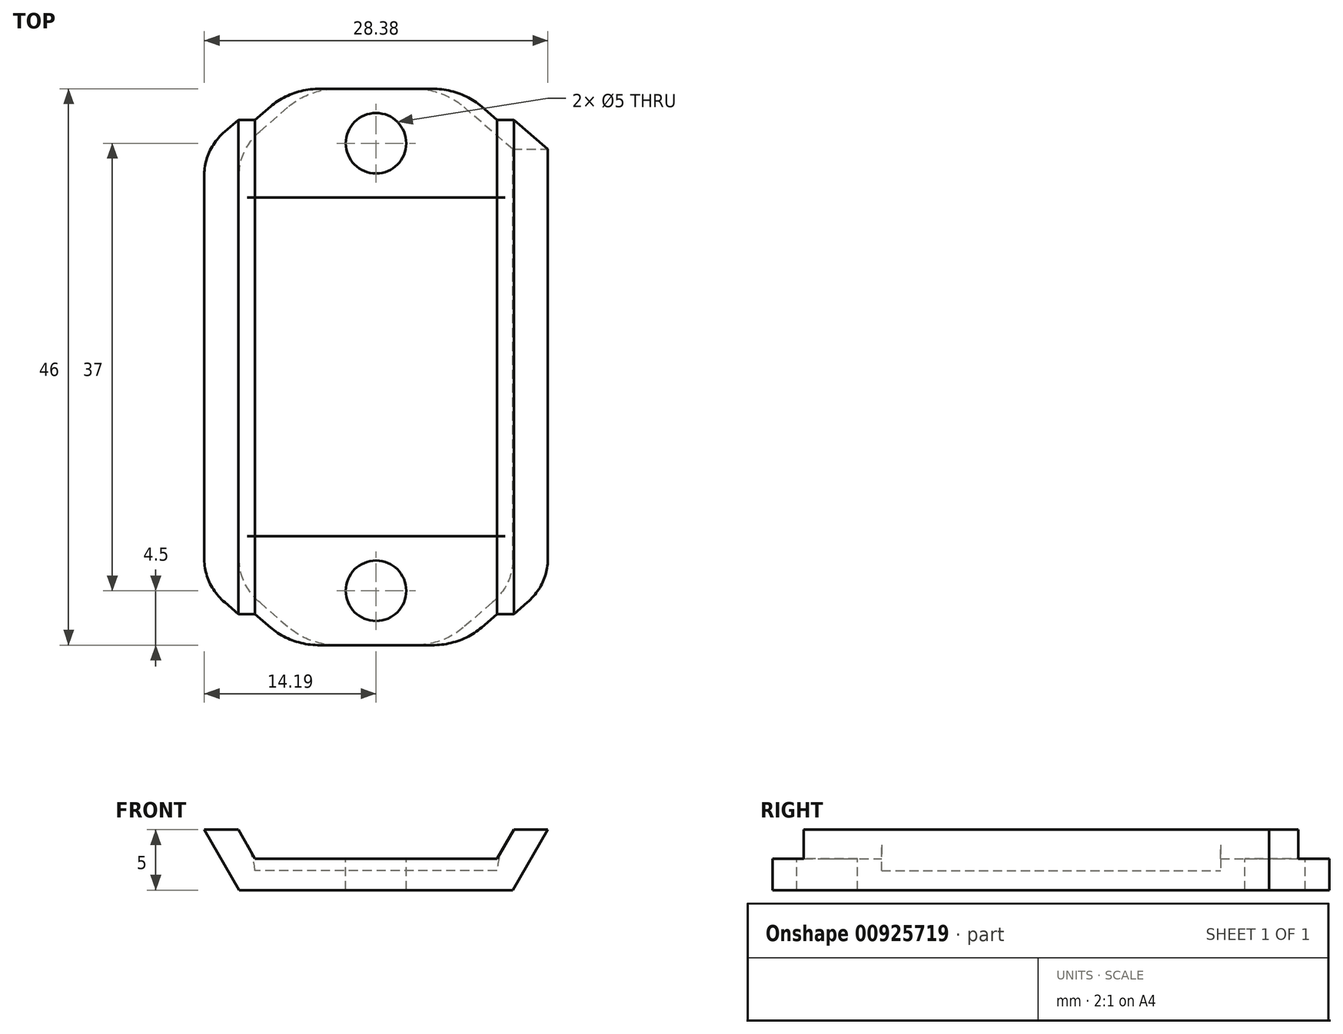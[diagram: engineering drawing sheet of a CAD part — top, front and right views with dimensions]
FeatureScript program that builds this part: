
annotation { "Feature Type Name" : "Feature", "Feature Type Description" : "" }
export const myFeature = defineFeature(function(context is Context, id is Id, definition is map)
    precondition{}
    {
        {
            var Q0;
            Q0=qCreatedBy(makeId("Front.planeOp"),FACE);
            var sketch = newSketch(context, id + "F0", { "sketchPlane" : qUnion([Q0])});
            skLineSegment(sketch, "E0", {"start": v(0, 0) * mm, "end": v(-11.3, 0) * mm});
            skLineSegment(sketch, "E1", {"start": v(-11.3, 0) * mm, "end": v(-14.19, 5) * mm});
            skLineSegment(sketch, "E2", {"start": v(-14.19, 5) * mm, "end": v(-11.39, 5) * mm});
            skLineSegment(sketch, "E3", {"start": v(-11.39, 5) * mm, "end": v(-10, 2.6) * mm});
            skLineSegment(sketch, "E4", {"start": v(-10, 2.6) * mm, "end": v(0, 2.6) * mm});
            skLineSegment(sketch, "E5", {"start": v(0, -9.75) * mm, "end": v(0, 12.13) * mm, "construction": true});
            skLineSegment(sketch, "E6.MirrorCS", {"start": v(10, 2.6) * mm, "end": v(0, 2.6) * mm});
            skLineSegment(sketch, "E7.MirrorCS", {"start": v(11.39, 5) * mm, "end": v(10, 2.6) * mm});
            skLineSegment(sketch, "E8.MirrorCS", {"start": v(14.19, 5) * mm, "end": v(11.39, 5) * mm});
            skLineSegment(sketch, "E9.MirrorCS", {"start": v(11.3, 0) * mm, "end": v(14.19, 5) * mm});
            skLineSegment(sketch, "E10.MirrorCS", {"start": v(0, 0) * mm, "end": v(11.3, 0) * mm});
            skSolve(sketch);
        }
        {
            var Q0;
            Q0=makeQuery(id+"F0.imprint","IMPRINT",FACE,{"disambiguationData":[TD([[makeQuery(id+"F0.imprint","IMPRINT",EDGE,{"derivedFrom":sQuery(id+"F0.wireOp",EDGE,"E0")}),-1.0]])]});
            extrude(context, id + "F1", {"entities" : qUnion([Q0]), "endBound" : BoundingType.SYMMETRIC, "depth" : 2 * (13 * mm + 10 * mm), "offsetDistance" : 25 * mm});
        }
        {
            var Q0;
            Q0=makeQuery(id+"F1.opExtrude","SWEPT_FACE",FACE,{"disambiguationData":[OSD([sQuery(id+"F0.wireOp",EDGE,"E4"),sQuery(id+"F0.wireOp",EDGE,"E6.MirrorCS")])]});
            var sketch = newSketch(context, id + "F2", { "sketchPlane" : qUnion([Q0])});
            skLineSegment(sketch, "E11.bottom", {"start": v(10, 14) * mm, "end": v(-10, 14) * mm});
            skLineSegment(sketch, "E11.top", {"start": v(10, -14) * mm, "end": v(-10, -14) * mm});
            skLineSegment(sketch, "E11.left", {"start": v(10, 14) * mm, "end": v(10, -14) * mm});
            skLineSegment(sketch, "E11.right", {"start": v(-10, 14) * mm, "end": v(-10, -14) * mm});
            skPoint(sketch, "E11.middle", {"position": v(0, 0) * mm});
            skLineSegment(sketch, "E12", {"start": v(-10, 23) * mm, "end": v(10, 14) * mm, "construction": true});
            skPoint(sketch, "E13", {"position": v(0, 18.5) * mm});
            skLineSegment(sketch, "E14", {"start": v(10, -14) * mm, "end": v(-10, -23) * mm, "construction": true});
            skPoint(sketch, "E15", {"position": v(0, -18.5) * mm});
            skSolve(sketch);
        }
        {
            var Q0;
            Q0=makeQuery(id+"F2.imprint","IMPRINT",FACE,{"disambiguationData":[TD([[makeQuery(id+"F2.imprint","IMPRINT",EDGE,{"derivedFrom":sQuery(id+"F2.wireOp",EDGE,"E11.bottom")}),1.0]])]});
            extrude(context, id + "F3", {"entities" : qUnion([Q0]), "operationType" : NewBodyOperationType.REMOVE, "oppositeDirection" : true, "depth" : 1 * mm, "offsetDistance" : 25 * mm});
        }
        {
            var Q0;
            Q0=sQuery(id+"F2.wireOp",VERTEX,"E15");
            var Q1;
            Q1=sQuery(id+"F2.wireOp",VERTEX,"E13");
            var Q2;
            Q2=makeQuery(id+"F1.opExtrude","SWEPT_BODY",BODY,{"disambiguationData":[OSD([sQuery(id+"F0.wireOp",EDGE,"E0"),sQuery(id+"F0.wireOp",EDGE,"E1"),sQuery(id+"F0.wireOp",EDGE,"E2"),sQuery(id+"F0.wireOp",EDGE,"E3"),sQuery(id+"F0.wireOp",EDGE,"E4"),sQuery(id+"F0.wireOp",EDGE,"E6.MirrorCS"),sQuery(id+"F0.wireOp",EDGE,"E7.MirrorCS"),sQuery(id+"F0.wireOp",EDGE,"E8.MirrorCS"),sQuery(id+"F0.wireOp",EDGE,"E9.MirrorCS"),sQuery(id+"F0.wireOp",EDGE,"E10.MirrorCS")])]});
            hole(context, id + "F4", {"style" : HoleStyle.SIMPLE, "endStyle" : HoleEndStyle.THROUGH, "holeDiameter" : 5 * mm, "majorDiameter" : 5 * mm, "isTappedThrough" : true, "tappedDepth" : 12 * mm, "tapClearance" : 3, "locations" : qUnion([Q0, Q1]), "scope" : qUnion([Q2])});
        }
        {
            var Q0;
            Q0=makeQuery(id+"F1.opExtrude","CAP_EDGE",EDGE,{"disambiguationData":[OSD([sQuery(id+"F0.wireOp",EDGE,"E1")])],"isStart":false});
            var Q1;
            Q1=makeQuery(id+"F1.opExtrude","CAP_EDGE",EDGE,{"disambiguationData":[OSD([sQuery(id+"F0.wireOp",EDGE,"E9.MirrorCS")])],"isStart":false});
            var Q2;
            Q2=makeQuery(id+"F1.opExtrude","CAP_EDGE",EDGE,{"disambiguationData":[OSD([sQuery(id+"F0.wireOp",EDGE,"E1")])],"isStart":true});
            var Q3;
            Q3=makeQuery(id+"F1.opExtrude","CAP_EDGE",EDGE,{"disambiguationData":[OSD([sQuery(id+"F0.wireOp",EDGE,"E9.MirrorCS")])],"isStart":true});
            chamfer(context, id + "F5", {"entities" : qUnion([Q0, Q1, Q2, Q3]), "width" : 5 * mm, "tangentPropagation" : true});
        }
        {
            var Q0;
            Q0=makeQuery(id+"F3.boolean.opBoolean","MERGE",EDGE,{"derivedFrom":[makeQuery(id+"F1.opExtrude","SWEPT_EDGE",EDGE,{"disambiguationData":[OSD([sQuery(id+"F0.wireOp",EDGE,"E3"),sQuery(id+"F0.wireOp",EDGE,"E4")])]})],"fromTools":[makeQuery(id+"F3.opExtrude","CAP_EDGE",EDGE,{"disambiguationData":[OSD([sQuery(id+"F2.wireOp",EDGE,"E11.right")])],"isStart":true})]});
            var Q1;
            Q1=makeQuery(id+"F3.boolean.opBoolean","MERGE",EDGE,{"derivedFrom":[makeQuery(id+"F1.opExtrude","SWEPT_EDGE",EDGE,{"disambiguationData":[OSD([sQuery(id+"F0.wireOp",EDGE,"E6.MirrorCS"),sQuery(id+"F0.wireOp",EDGE,"E7.MirrorCS")])]})],"fromTools":[makeQuery(id+"F3.opExtrude","CAP_EDGE",EDGE,{"disambiguationData":[OSD([sQuery(id+"F2.wireOp",EDGE,"E11.left")])],"isStart":true})]});
            var Q2;
            {var subQ0=sQuery(id+"F0.wireOp",EDGE,"E1");Q2=makeQuery(id+"F5.opChamfer","BLEND_EDGE",EDGE,{"blendedFrom":[makeQuery(id+"F1.opExtrude","CAP_EDGE",EDGE,{"disambiguationData":[OSD([subQ0])],"isStart":true}),makeQuery(id+"F1.opExtrude","CAP_FACE",FACE,{"disambiguationData":[OSD([sQuery(id+"F0.wireOp",EDGE,"E0"),subQ0,sQuery(id+"F0.wireOp",EDGE,"E2"),sQuery(id+"F0.wireOp",EDGE,"E3"),sQuery(id+"F0.wireOp",EDGE,"E4"),sQuery(id+"F0.wireOp",EDGE,"E6.MirrorCS"),sQuery(id+"F0.wireOp",EDGE,"E7.MirrorCS"),sQuery(id+"F0.wireOp",EDGE,"E8.MirrorCS"),sQuery(id+"F0.wireOp",EDGE,"E9.MirrorCS"),sQuery(id+"F0.wireOp",EDGE,"E10.MirrorCS")])],"isStart":true})],"blendedInto":[makeQuery(id+"F1.opExtrude","CAP_FACE",FACE,{"disambiguationData":[OSD([sQuery(id+"F0.wireOp",EDGE,"E0"),subQ0,sQuery(id+"F0.wireOp",EDGE,"E2"),sQuery(id+"F0.wireOp",EDGE,"E3"),sQuery(id+"F0.wireOp",EDGE,"E4"),sQuery(id+"F0.wireOp",EDGE,"E6.MirrorCS"),sQuery(id+"F0.wireOp",EDGE,"E7.MirrorCS"),sQuery(id+"F0.wireOp",EDGE,"E8.MirrorCS"),sQuery(id+"F0.wireOp",EDGE,"E9.MirrorCS"),sQuery(id+"F0.wireOp",EDGE,"E10.MirrorCS")])],"isStart":true})]});}
            var Q3;
            {var subQ0=sQuery(id+"F0.wireOp",EDGE,"E9.MirrorCS");Q3=makeQuery(id+"F5.opChamfer","BLEND_EDGE",EDGE,{"blendedFrom":[makeQuery(id+"F1.opExtrude","CAP_EDGE",EDGE,{"disambiguationData":[OSD([subQ0])],"isStart":true}),makeQuery(id+"F1.opExtrude","CAP_FACE",FACE,{"disambiguationData":[OSD([sQuery(id+"F0.wireOp",EDGE,"E0"),sQuery(id+"F0.wireOp",EDGE,"E1"),sQuery(id+"F0.wireOp",EDGE,"E2"),sQuery(id+"F0.wireOp",EDGE,"E3"),sQuery(id+"F0.wireOp",EDGE,"E4"),sQuery(id+"F0.wireOp",EDGE,"E6.MirrorCS"),sQuery(id+"F0.wireOp",EDGE,"E7.MirrorCS"),sQuery(id+"F0.wireOp",EDGE,"E8.MirrorCS"),subQ0,sQuery(id+"F0.wireOp",EDGE,"E10.MirrorCS")])],"isStart":true})],"blendedInto":[makeQuery(id+"F1.opExtrude","CAP_FACE",FACE,{"disambiguationData":[OSD([sQuery(id+"F0.wireOp",EDGE,"E0"),sQuery(id+"F0.wireOp",EDGE,"E1"),sQuery(id+"F0.wireOp",EDGE,"E2"),sQuery(id+"F0.wireOp",EDGE,"E3"),sQuery(id+"F0.wireOp",EDGE,"E4"),sQuery(id+"F0.wireOp",EDGE,"E6.MirrorCS"),sQuery(id+"F0.wireOp",EDGE,"E7.MirrorCS"),sQuery(id+"F0.wireOp",EDGE,"E8.MirrorCS"),subQ0,sQuery(id+"F0.wireOp",EDGE,"E10.MirrorCS")])],"isStart":true})]});}
            var Q4;
            {var subQ0=sQuery(id+"F0.wireOp",EDGE,"E1");Q4=makeQuery(id+"F5.opChamfer","BLEND_EDGE",EDGE,{"blendedFrom":[makeQuery(id+"F1.opExtrude","CAP_EDGE",EDGE,{"disambiguationData":[OSD([subQ0])],"isStart":true}),makeQuery(id+"F1.opExtrude","SWEPT_FACE",FACE,{"disambiguationData":[OSD([subQ0])]})],"blendedInto":[makeQuery(id+"F1.opExtrude","SWEPT_FACE",FACE,{"disambiguationData":[OSD([subQ0])]})]});}
            var Q5;
            {var subQ0=sQuery(id+"F0.wireOp",EDGE,"E9.MirrorCS");Q5=makeQuery(id+"F5.opChamfer","BLEND_EDGE",EDGE,{"blendedFrom":[makeQuery(id+"F1.opExtrude","CAP_EDGE",EDGE,{"disambiguationData":[OSD([subQ0])],"isStart":false}),makeQuery(id+"F1.opExtrude","SWEPT_FACE",FACE,{"disambiguationData":[OSD([subQ0])]})],"blendedInto":[makeQuery(id+"F1.opExtrude","SWEPT_FACE",FACE,{"disambiguationData":[OSD([subQ0])]})]});}
            var Q6;
            {var subQ0=sQuery(id+"F0.wireOp",EDGE,"E9.MirrorCS");Q6=makeQuery(id+"F5.opChamfer","BLEND_EDGE",EDGE,{"blendedFrom":[makeQuery(id+"F1.opExtrude","CAP_EDGE",EDGE,{"disambiguationData":[OSD([subQ0])],"isStart":false}),makeQuery(id+"F1.opExtrude","CAP_FACE",FACE,{"disambiguationData":[OSD([sQuery(id+"F0.wireOp",EDGE,"E0"),sQuery(id+"F0.wireOp",EDGE,"E1"),sQuery(id+"F0.wireOp",EDGE,"E2"),sQuery(id+"F0.wireOp",EDGE,"E3"),sQuery(id+"F0.wireOp",EDGE,"E4"),sQuery(id+"F0.wireOp",EDGE,"E6.MirrorCS"),sQuery(id+"F0.wireOp",EDGE,"E7.MirrorCS"),sQuery(id+"F0.wireOp",EDGE,"E8.MirrorCS"),subQ0,sQuery(id+"F0.wireOp",EDGE,"E10.MirrorCS")])],"isStart":false})],"blendedInto":[makeQuery(id+"F1.opExtrude","CAP_FACE",FACE,{"disambiguationData":[OSD([sQuery(id+"F0.wireOp",EDGE,"E0"),sQuery(id+"F0.wireOp",EDGE,"E1"),sQuery(id+"F0.wireOp",EDGE,"E2"),sQuery(id+"F0.wireOp",EDGE,"E3"),sQuery(id+"F0.wireOp",EDGE,"E4"),sQuery(id+"F0.wireOp",EDGE,"E6.MirrorCS"),sQuery(id+"F0.wireOp",EDGE,"E7.MirrorCS"),sQuery(id+"F0.wireOp",EDGE,"E8.MirrorCS"),subQ0,sQuery(id+"F0.wireOp",EDGE,"E10.MirrorCS")])],"isStart":false})]});}
            var Q7;
            {var subQ0=sQuery(id+"F0.wireOp",EDGE,"E1");Q7=makeQuery(id+"F5.opChamfer","BLEND_EDGE",EDGE,{"blendedFrom":[makeQuery(id+"F1.opExtrude","CAP_EDGE",EDGE,{"disambiguationData":[OSD([subQ0])],"isStart":false}),makeQuery(id+"F1.opExtrude","CAP_FACE",FACE,{"disambiguationData":[OSD([sQuery(id+"F0.wireOp",EDGE,"E0"),subQ0,sQuery(id+"F0.wireOp",EDGE,"E2"),sQuery(id+"F0.wireOp",EDGE,"E3"),sQuery(id+"F0.wireOp",EDGE,"E4"),sQuery(id+"F0.wireOp",EDGE,"E6.MirrorCS"),sQuery(id+"F0.wireOp",EDGE,"E7.MirrorCS"),sQuery(id+"F0.wireOp",EDGE,"E8.MirrorCS"),sQuery(id+"F0.wireOp",EDGE,"E9.MirrorCS"),sQuery(id+"F0.wireOp",EDGE,"E10.MirrorCS")])],"isStart":false})],"blendedInto":[makeQuery(id+"F1.opExtrude","CAP_FACE",FACE,{"disambiguationData":[OSD([sQuery(id+"F0.wireOp",EDGE,"E0"),subQ0,sQuery(id+"F0.wireOp",EDGE,"E2"),sQuery(id+"F0.wireOp",EDGE,"E3"),sQuery(id+"F0.wireOp",EDGE,"E4"),sQuery(id+"F0.wireOp",EDGE,"E6.MirrorCS"),sQuery(id+"F0.wireOp",EDGE,"E7.MirrorCS"),sQuery(id+"F0.wireOp",EDGE,"E8.MirrorCS"),sQuery(id+"F0.wireOp",EDGE,"E9.MirrorCS"),sQuery(id+"F0.wireOp",EDGE,"E10.MirrorCS")])],"isStart":false})]});}
            var Q8;
            {var subQ0=sQuery(id+"F0.wireOp",EDGE,"E1");Q8=makeQuery(id+"F5.opChamfer","BLEND_EDGE",EDGE,{"blendedFrom":[makeQuery(id+"F1.opExtrude","CAP_EDGE",EDGE,{"disambiguationData":[OSD([subQ0])],"isStart":false}),makeQuery(id+"F1.opExtrude","SWEPT_FACE",FACE,{"disambiguationData":[OSD([subQ0])]})],"blendedInto":[makeQuery(id+"F1.opExtrude","SWEPT_FACE",FACE,{"disambiguationData":[OSD([subQ0])]})]});}
            fillet(context, id + "F6", {"entities" : qUnion([Q0, Q1, Q2, Q3, Q4, Q5, Q6, Q7, Q8]), "tangentPropagation" : true, "radius" : 5 * mm, "defaultsChanged" : false, "vertexSettings" : [], "allowEdgeOverflow" : false});
        }
    });
